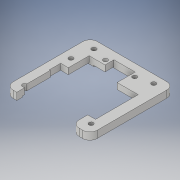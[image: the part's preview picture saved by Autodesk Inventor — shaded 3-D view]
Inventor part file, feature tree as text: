
AUTODESK INVENTOR PART (.ipt)
format: ipt  version: 2019 (Build 230136000, 136)  size: 227,328 bytes
history: native  units: in
note: dims shown in document units (in); Inventor stores cm internally (conversion verified against a paired STEP export)
features: extrude x5, sketch x4, fillet x2
ambient origin geometry x8: Origin, YZ Plane, XZ Plane, XY Plane, X Axis, Y Axis, Z Axis, Center Point
bodies: Solid1 (feature_tree)
feature tree (11):
  sketch  "Sketch1"  dims[d0=2.3622in d2=2.2114in d4=1.2894in d7=0.2451in]
  extrude  "Extrusion1"  Depth=2.2114in
  extrude  "Extrusion3"  Depth=0.122in
  extrude  "Extrusion2"  Depth=0.2431in
  fillet  "Fillet1"  Radius=0.2874in
  fillet  "Fillet2"  Radius=0.5047in
  extrude  "Extrusion4"  Depth=0.3051in
  extrude  "Extrusion5"  Depth=0.4331in
  sketch  "Sketch2"  dims[d8=0.7814in d9=0.122in]
  sketch  "Sketch3"  dims[d12=0.5071in d14=0.2431in d15=0.2874in d16=0.5047in]
  sketch  "Sketch4"  dims[d17=0.4451in d18=0.4906in d19=0.4331in d21=1.0443in d22=1.361in d25=1.9172in d27=0.2165in d28=0.2431in d30=0.2874in d31=0.4614in d32=0.2in d33=0.0in d34=0.122in d35=0.122in d36=0.122in d38=0.3364in d39=0.7681in d40=0.122in d41=0.3364in d42=0.7681in d43=2.0864in d44=0.2431in d46=0.3in d47=0.0in d52=2.12in d53=2.0in d54=0.0312in d55=0.0in d56=0.2in d57=0.2in d58=0.441in d59=0.441in d60=0.191in d61=0.191in d64=0.25in d65=0.0312in d66=0.0in d79=0.125in d80=0.0in d170=0.15in d171=0.15in d172=0.125in d173=0.2305in d174=0.2795in d176=0.2148in d177=0.3051in]
